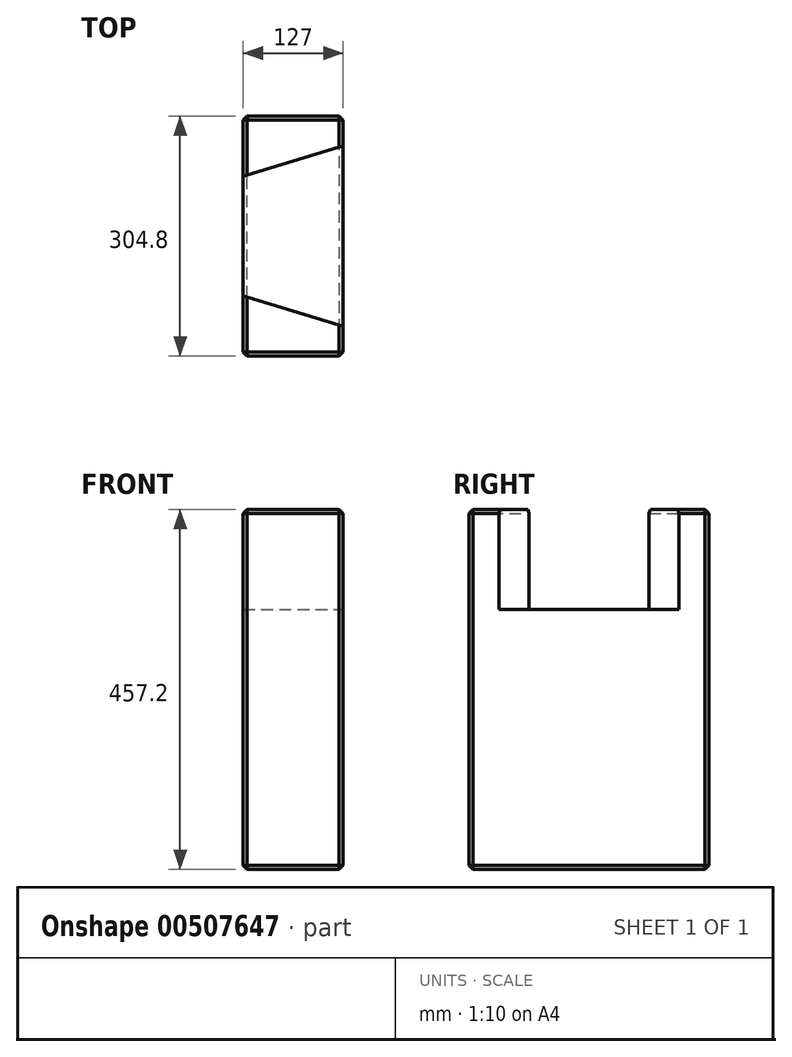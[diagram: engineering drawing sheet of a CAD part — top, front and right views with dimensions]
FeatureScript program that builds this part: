
annotation { "Feature Type Name" : "Feature", "Feature Type Description" : "" }
export const myFeature = defineFeature(function(context is Context, id is Id, definition is map)
    precondition{}
    {
        {
            var Q0;
            Q0=qCreatedBy(makeId("Right.planeOp"),FACE);
            var sketch = newSketch(context, id + "F0", { "sketchPlane" : qUnion([Q0])});
            skLineSegment(sketch, "E0.bottom", {"start": v(-152.4, 228.6) * mm, "end": v(152.4, 228.6) * mm});
            skLineSegment(sketch, "E0.top", {"start": v(-152.4, -228.6) * mm, "end": v(152.4, -228.6) * mm});
            skLineSegment(sketch, "E0.left", {"start": v(-152.4, 228.6) * mm, "end": v(-152.4, -228.6) * mm});
            skLineSegment(sketch, "E0.right", {"start": v(152.4, 228.6) * mm, "end": v(152.4, -228.6) * mm});
            skSolve(sketch);
        }
        {
            var Q0;
            Q0 = qSketchRegion(id + "F0", true);
            extrude(context, id + "F1", {"entities" : qUnion([Q0]), "depth" : 63.5 * mm, "hasSecondDirection" : true, "secondDirectionOppositeDirection" : true, "secondDirectionDepth" : 63.5 * mm});
        }
        {
            var Q0;
            Q0=makeQuery(id+"F1.opExtrude","SWEPT_FACE",FACE,{"disambiguationData":[OSD([sQuery(id+"F0.wireOp",EDGE,"E0.bottom")])]});
            var sketch = newSketch(context, id + "F2", { "sketchPlane" : qUnion([Q0])});
            skLineSegment(sketch, "E1", {"start": v(-63.5, 0) * mm, "end": v(-63.5, -76.2) * mm});
            skLineSegment(sketch, "E2", {"start": v(-63.5, -76.2) * mm, "end": v(63.5, -114.3) * mm});
            skLineSegment(sketch, "E3", {"start": v(63.5, -114.3) * mm, "end": v(63.5, 0) * mm});
            skLineSegment(sketch, "E4.MirrorCS", {"start": v(-63.5, 0) * mm, "end": v(-63.5, 76.2) * mm});
            skLineSegment(sketch, "E5.MirrorCS", {"start": v(-63.5, 76.2) * mm, "end": v(63.5, 114.3) * mm});
            skLineSegment(sketch, "E6.MirrorCS", {"start": v(63.5, 114.3) * mm, "end": v(63.5, 0) * mm});
            skSolve(sketch);
        }
        {
            var Q0;
            Q0 = qSketchRegion(id + "F2", true);
            extrude(context, id + "F3", {"entities" : qUnion([Q0]), "operationType" : NewBodyOperationType.REMOVE, "oppositeDirection" : true, "depth" : 127 * mm});
        }
        {
            var Q0;
            Q0=makeQuery(id+"F1.opExtrude","CAP_EDGE",EDGE,{"disambiguationData":[OSD([sQuery(id+"F0.wireOp",EDGE,"E0.right")])],"isStart":false});
            var Q1;
            {var subQ0=sQuery(id+"F0.wireOp",EDGE,"E0.bottom");var subQ1=sQuery(id+"F0.wireOp",EDGE,"E0.right");Q1=makeQuery(id+"F3.boolean.opBoolean","SPLIT",EDGE,{"disambiguationData":[TD([makeQuery(id+"F1.opExtrude","SWEPT_FACE",FACE,{"disambiguationData":[OSD([subQ1])]})])],"derivedFrom":makeQuery(id+"F1.opExtrude","CAP_EDGE",EDGE,{"disambiguationData":[OSD([subQ0])],"isStart":false})});}
            var Q2;
            Q2=makeQuery(id+"F3.boolean.opBoolean","COPY",EDGE,{"derivedFrom":makeQuery(id+"F3.opExtrude","SWEPT_EDGE",EDGE,{"disambiguationData":[OSD([sQuery(id+"F0.wireOp",EDGE,"E0.bottom"),sQuery(id+"F2.wireOp",EDGE,"E5.MirrorCS"),sQuery(id+"F2.wireOp",EDGE,"E6.MirrorCS")])]})});
            var Q3;
            Q3=makeQuery(id+"F3.boolean.opBoolean","COPY",EDGE,{"derivedFrom":makeQuery(id+"F3.opExtrude","CAP_EDGE",EDGE,{"disambiguationData":[OSD([sQuery(id+"F2.wireOp",EDGE,"E3"),sQuery(id+"F2.wireOp",EDGE,"E6.MirrorCS")])],"isStart":false})});
            var Q4;
            Q4=makeQuery(id+"F3.boolean.opBoolean","COPY",EDGE,{"derivedFrom":makeQuery(id+"F3.opExtrude","SWEPT_EDGE",EDGE,{"disambiguationData":[OSD([sQuery(id+"F0.wireOp",EDGE,"E0.bottom"),sQuery(id+"F2.wireOp",EDGE,"E2"),sQuery(id+"F2.wireOp",EDGE,"E3")])]})});
            var Q5;
            {var subQ0=sQuery(id+"F0.wireOp",EDGE,"E0.bottom");var subQ1=sQuery(id+"F0.wireOp",EDGE,"E0.left");Q5=makeQuery(id+"F3.boolean.opBoolean","SPLIT",EDGE,{"disambiguationData":[TD([makeQuery(id+"F1.opExtrude","SWEPT_FACE",FACE,{"disambiguationData":[OSD([subQ1])]})])],"derivedFrom":makeQuery(id+"F1.opExtrude","CAP_EDGE",EDGE,{"disambiguationData":[OSD([subQ0])],"isStart":false})});}
            var Q6;
            Q6=makeQuery(id+"F1.opExtrude","CAP_EDGE",EDGE,{"disambiguationData":[OSD([sQuery(id+"F0.wireOp",EDGE,"E0.left")])],"isStart":false});
            var Q7;
            Q7=makeQuery(id+"F1.opExtrude","CAP_EDGE",EDGE,{"disambiguationData":[OSD([sQuery(id+"F0.wireOp",EDGE,"E0.top")])],"isStart":false});
            var Q8;
            Q8=makeQuery(id+"F1.opExtrude","SWEPT_EDGE",EDGE,{"disambiguationData":[OSD([sQuery(id+"F0.wireOp",EDGE,"E0.bottom"),sQuery(id+"F0.wireOp",EDGE,"E0.right")])]});
            var Q9;
            Q9=makeQuery(id+"F3.boolean.opBoolean","COPY",EDGE,{"derivedFrom":makeQuery(id+"F3.opExtrude","CAP_EDGE",EDGE,{"disambiguationData":[OSD([sQuery(id+"F2.wireOp",EDGE,"E5.MirrorCS")])],"isStart":true})});
            var Q10;
            Q10=makeQuery(id+"F3.boolean.opBoolean","COPY",EDGE,{"derivedFrom":makeQuery(id+"F3.opExtrude","CAP_EDGE",EDGE,{"disambiguationData":[OSD([sQuery(id+"F2.wireOp",EDGE,"E2")])],"isStart":true})});
            var Q11;
            Q11=makeQuery(id+"F1.opExtrude","SWEPT_EDGE",EDGE,{"disambiguationData":[OSD([sQuery(id+"F0.wireOp",EDGE,"E0.bottom"),sQuery(id+"F0.wireOp",EDGE,"E0.left")])]});
            var Q12;
            {var subQ0=sQuery(id+"F0.wireOp",EDGE,"E0.bottom");var subQ1=sQuery(id+"F0.wireOp",EDGE,"E0.left");Q12=makeQuery(id+"F3.boolean.opBoolean","SPLIT",EDGE,{"disambiguationData":[TD([makeQuery(id+"F1.opExtrude","SWEPT_FACE",FACE,{"disambiguationData":[OSD([subQ1])]})])],"derivedFrom":makeQuery(id+"F1.opExtrude","CAP_EDGE",EDGE,{"disambiguationData":[OSD([subQ0])],"isStart":true})});}
            var Q13;
            Q13=makeQuery(id+"F1.opExtrude","CAP_EDGE",EDGE,{"disambiguationData":[OSD([sQuery(id+"F0.wireOp",EDGE,"E0.left")])],"isStart":true});
            var Q14;
            Q14=makeQuery(id+"F1.opExtrude","CAP_EDGE",EDGE,{"disambiguationData":[OSD([sQuery(id+"F0.wireOp",EDGE,"E0.top")])],"isStart":true});
            var Q15;
            Q15=makeQuery(id+"F1.opExtrude","CAP_EDGE",EDGE,{"disambiguationData":[OSD([sQuery(id+"F0.wireOp",EDGE,"E0.right")])],"isStart":true});
            var Q16;
            {var subQ0=sQuery(id+"F0.wireOp",EDGE,"E0.bottom");var subQ1=sQuery(id+"F0.wireOp",EDGE,"E0.right");Q16=makeQuery(id+"F3.boolean.opBoolean","SPLIT",EDGE,{"disambiguationData":[TD([makeQuery(id+"F1.opExtrude","SWEPT_FACE",FACE,{"disambiguationData":[OSD([subQ1])]})])],"derivedFrom":makeQuery(id+"F1.opExtrude","CAP_EDGE",EDGE,{"disambiguationData":[OSD([subQ0])],"isStart":true})});}
            var Q17;
            Q17=makeQuery(id+"F3.boolean.opBoolean","COPY",EDGE,{"derivedFrom":makeQuery(id+"F3.opExtrude","SWEPT_EDGE",EDGE,{"disambiguationData":[OSD([sQuery(id+"F0.wireOp",EDGE,"E0.bottom"),sQuery(id+"F2.wireOp",EDGE,"E4.MirrorCS"),sQuery(id+"F2.wireOp",EDGE,"E5.MirrorCS")])]})});
            var Q18;
            Q18=makeQuery(id+"F3.boolean.opBoolean","COPY",EDGE,{"derivedFrom":makeQuery(id+"F3.opExtrude","CAP_EDGE",EDGE,{"disambiguationData":[OSD([sQuery(id+"F2.wireOp",EDGE,"E1"),sQuery(id+"F2.wireOp",EDGE,"E4.MirrorCS")])],"isStart":false})});
            var Q19;
            Q19=makeQuery(id+"F4.boolean.opBoolean","COPY",EDGE,{"derivedFrom":makeQuery(id+"F4.opExtrude","CAP_EDGE",EDGE,{"disambiguationData":[OSD([sQuery(id+"F27PzOWzq32fsxu_1.wireOp",EDGE,"toRrb1mX-NdyE-H1tD-Ad8Q-EnJrqZh5TOEX"),sQuery(id+"F27PzOWzq32fsxu_1.wireOp",EDGE,"381fca3e-a48b-4ae1-befe-e612c4f6395a0.MirrorCS")])],"isStart":false})});
            var Q20;
            Q20=makeQuery(id+"F4.boolean.opBoolean","COPY",EDGE,{"derivedFrom":makeQuery(id+"F4.opExtrude","SWEPT_EDGE",EDGE,{"disambiguationData":[OSD([sQuery(id+"F0.wireOp",EDGE,"E0.top"),sQuery(id+"F27PzOWzq32fsxu_1.wireOp",EDGE,"bdf538ec-da29-4b88-84af-ef410b189a720.MirrorCS"),sQuery(id+"F27PzOWzq32fsxu_1.wireOp",EDGE,"381fca3e-a48b-4ae1-befe-e612c4f6395a0.MirrorCS")])]})});
            var Q21;
            Q21=makeQuery(id+"F4.boolean.opBoolean","COPY",EDGE,{"derivedFrom":makeQuery(id+"F4.opExtrude","CAP_EDGE",EDGE,{"disambiguationData":[OSD([sQuery(id+"F27PzOWzq32fsxu_1.wireOp",EDGE,"bdf538ec-da29-4b88-84af-ef410b189a720.MirrorCS")])],"isStart":true})});
            var Q22;
            Q22=makeQuery(id+"F4.boolean.opBoolean","COPY",EDGE,{"derivedFrom":makeQuery(id+"F4.opExtrude","SWEPT_EDGE",EDGE,{"disambiguationData":[OSD([sQuery(id+"F0.wireOp",EDGE,"E0.top"),sQuery(id+"F27PzOWzq32fsxu_1.wireOp",EDGE,"7b9436fb-b277-4288-8a8c-59b42d103edd0.MirrorCS"),sQuery(id+"F27PzOWzq32fsxu_1.wireOp",EDGE,"bdf538ec-da29-4b88-84af-ef410b189a720.MirrorCS")])]})});
            var Q23;
            Q23=makeQuery(id+"F4.boolean.opBoolean","COPY",EDGE,{"derivedFrom":makeQuery(id+"F4.opExtrude","CAP_EDGE",EDGE,{"disambiguationData":[OSD([sQuery(id+"F27PzOWzq32fsxu_1.wireOp",EDGE,"IswkgnwY-6BaU-Hux7-l57a-SIklBkQ91Nw8"),sQuery(id+"F27PzOWzq32fsxu_1.wireOp",EDGE,"7b9436fb-b277-4288-8a8c-59b42d103edd0.MirrorCS")])],"isStart":false})});
            var Q24;
            Q24=makeQuery(id+"F4.boolean.opBoolean","COPY",EDGE,{"derivedFrom":makeQuery(id+"F4.opExtrude","SWEPT_EDGE",EDGE,{"disambiguationData":[OSD([sQuery(id+"F0.wireOp",EDGE,"E0.top"),sQuery(id+"F27PzOWzq32fsxu_1.wireOp",EDGE,"IswkgnwY-6BaU-Hux7-l57a-SIklBkQ91Nw8"),sQuery(id+"F27PzOWzq32fsxu_1.wireOp",EDGE,"9pNBPaKO-rEmo-laPy-LPsd-v5zAeuvpM39h")])]})});
            var Q25;
            Q25=makeQuery(id+"F4.boolean.opBoolean","COPY",EDGE,{"derivedFrom":makeQuery(id+"F4.opExtrude","CAP_EDGE",EDGE,{"disambiguationData":[OSD([sQuery(id+"F27PzOWzq32fsxu_1.wireOp",EDGE,"9pNBPaKO-rEmo-laPy-LPsd-v5zAeuvpM39h")])],"isStart":true})});
            var Q26;
            Q26=makeQuery(id+"F4.boolean.opBoolean","COPY",EDGE,{"derivedFrom":makeQuery(id+"F4.opExtrude","SWEPT_EDGE",EDGE,{"disambiguationData":[OSD([sQuery(id+"F0.wireOp",EDGE,"E0.top"),sQuery(id+"F27PzOWzq32fsxu_1.wireOp",EDGE,"9pNBPaKO-rEmo-laPy-LPsd-v5zAeuvpM39h"),sQuery(id+"F27PzOWzq32fsxu_1.wireOp",EDGE,"toRrb1mX-NdyE-H1tD-Ad8Q-EnJrqZh5TOEX")])]})});
            var Q27;
            Q27=makeQuery(id+"F1.opExtrude","SWEPT_EDGE",EDGE,{"disambiguationData":[OSD([sQuery(id+"F0.wireOp",EDGE,"E0.top"),sQuery(id+"F0.wireOp",EDGE,"E0.right")])]});
            var Q28;
            Q28=makeQuery(id+"F1.opExtrude","SWEPT_EDGE",EDGE,{"disambiguationData":[OSD([sQuery(id+"F0.wireOp",EDGE,"E0.top"),sQuery(id+"F0.wireOp",EDGE,"E0.left")])]});
            chamfer(context, id + "F5", {"entities" : qUnion([Q0, Q1, Q2, Q3, Q4, Q5, Q6, Q7, Q8, Q9, Q10, Q11, Q12, Q13, Q14, Q15, Q16, Q17, Q18, Q19, Q20, Q21, Q22, Q23, Q24, Q25, Q26, Q27, Q28]), "width" : 5.08 * mm, "tangentPropagation" : true});
        }
    });
